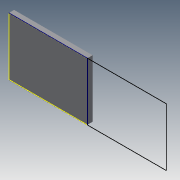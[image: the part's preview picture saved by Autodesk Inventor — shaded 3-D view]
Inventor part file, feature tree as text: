
AUTODESK INVENTOR PART (.ipt)
format: ipt  version: 2015 (Build 190159000, 159)  size: 85,504 bytes
history: native  units: mm
features: other x5, sketch x2, extrude x1, projected_geometry x1
ambient origin geometry x8: Origin, YZ Plane, XZ Plane, XY Plane, X Axis, Y Axis, Z Axis, Center Point
bodies: Solid1 (feature_tree)
feature tree (9):
  other  "Blocks"
  extrude  "Extrusion1"  Depth=150.0mm
  sketch  "Sketch2"  dims[d2=10.0mm d3=0.0mm]
  other  "DXF"
  sketch  "Sketch1"  dims[d0=110.0mm d1=150.0mm]
  projected_geometry  "Projected Loop1"
  other  "Block1"
  other  "Block1:1"
  other  "Block1:2"
